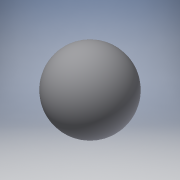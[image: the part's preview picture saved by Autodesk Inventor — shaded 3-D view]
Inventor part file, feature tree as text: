
AUTODESK INVENTOR PART (.ipt)
format: ipt  version: 2019 (Build 230136000, 136)  size: 122,880 bytes
history: native  units: in
note: dims shown in document units (in); Inventor stores cm internally (conversion verified against a paired STEP export)
features: revolve x1, sketch x1
ambient origin geometry x8: Origin, YZ Plane, XZ Plane, XY Plane, X Axis, Y Axis, Z Axis, Center Point
bodies: Solid1 (feature_tree)
feature tree (2):
  revolve  "Revolution1"  [1 undecoded]
  sketch  "Sketch1"  dims[d0=2.5in d1=1.25in d2=90.0deg]
note: 1 required parameter value undecoded (feature->parameter linkage not recoverable at this tier; creation-order binding heuristic only, values carry confidence <= 0.55)
